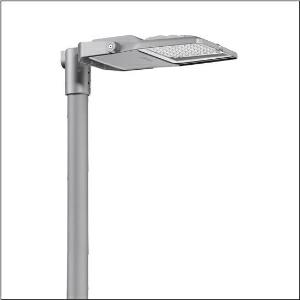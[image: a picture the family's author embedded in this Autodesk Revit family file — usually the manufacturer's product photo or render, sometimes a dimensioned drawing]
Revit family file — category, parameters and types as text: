
# Revit family: floodlight_fl_21_iq_mini___pl33t_5xa7771b4f3a_1cb2
name_source: partatom
category: Lighting Fixtures
units: mm (PartAtom-declared; Revit-internal decimal feet)

## family parameters
Cut with Voids When Loaded = No
Host = Face
Light Source = No
Part Type = Normal
Room Calculation Point = No
Round Connector Dimension = Use Diameter
Shared = No

## types (1)
- --- (1 x LED, 6420 lm, 45.5 W, 4000K)
    Apparent Load = 46 VA
    CIE Flux Codes = 26 75 99 100 100
    Color Rendering = 70
    Color Temperature = 4000K
    Default Elevation = 1800 mm
    Description = Floodlight FL 21 iQ mini, floodlight, primary light control with lens, of PMMA, primary optical cover: protective disc, of toughened safety glass, transparent, light distribution: PL33T, light emission: direct distribution, installation type: surface-mounted, LED, High Power LED, rated luminous flux: 6.420lm, luminous efficacy: 141lm/W, light colour: 740, colour temperature: 4000K, control: Auto-Match, Temp-Guard, Lumen-Switch, Night-Set, Smart-Wire, Light-Fading, Desk-Remote (wireless, voltage-free reading and setting of iQ features in the workshop via application-optimized NFC function/RFID function), optimised constant luminous flux control (CLO 2.0), with terminal, 6-pole, mains connection: 220..240V, AC, 50/60Hz, start of lifetime: 46W, end of service life: 48W, reduction: 22W, luminaire housing, of diecast aluminium, powder-coated, Siteco® metallic grey (DB 702S), corrosivity category C5 mid according to DIN EN ISO 12944, sealing non-destructively replaceable, please order mast flange separately, mast bracket, of steel, galvanised, powder-coated, Siteco® metallic grey (DB 702S), protection rating (complete): IP66, insulation class (complete): insulation class II (safety insulation), certification: CE, ENEC, VDE, protection symbol: D, impact resistance: IK08, permissible operating ambient temperature: -40..+40°C, permissible operating ambient temperature for outdoor applications: -40..+50°C, standard: DIN EN 12944, LABS conformity tested according to VDMA 24364:2018-05, packaging unit: 1 piece

Light Distribution: PL33T
    Height = 70 mm
    Lamp = 1 x LED
    Lamp Light Flux = 6420 lm
    Lamp Power = 45.5 W
    Lamp count = 1
    Length = 485 mm
    Luminous efficacy = 141 lm/W
    Manufacturer = Siteco
    ModVariant = No
    Model = 5XA7771B4F3A
    Number of Poles = 1
    OnlyDefault = Yes
    Power Factor = 1
    Product Name = Floodlight FL 21 iQ mini | PL33T
    Product group = floodlight | pylon annexe
    ProductGroupID = 6200
    Protection Class = Protection class II
    Protection Degree = IP 66
    RLX_Detail_Level = 1
    RLX_Emergency_Light_Flux = 0 lm
    RLX_Emergency_Type = 0
    RLX_Emergency_Type_DB = No
    RlxData = <blob elided: 101005 chars, md5=d61bab66>
    Socket = socket
    Standby Power = 0 W
    System Light Flux = 6420 lm
    System Power = 46 W
    Type Comments = factory setting: luminous flux: 100 % | dim-lin: 254 | 463 mA
    Type Image = l_1007125.jpg
    URL = http://relux.com
    VarID = @adj_082659
    Voltage = 0 V
    Weight = 0.00 kg
    Width = 337 mm

## geometry (parser evidence)
native form markers: Blend x4, Sweep x11
no freeform markers — native parametric forms only
